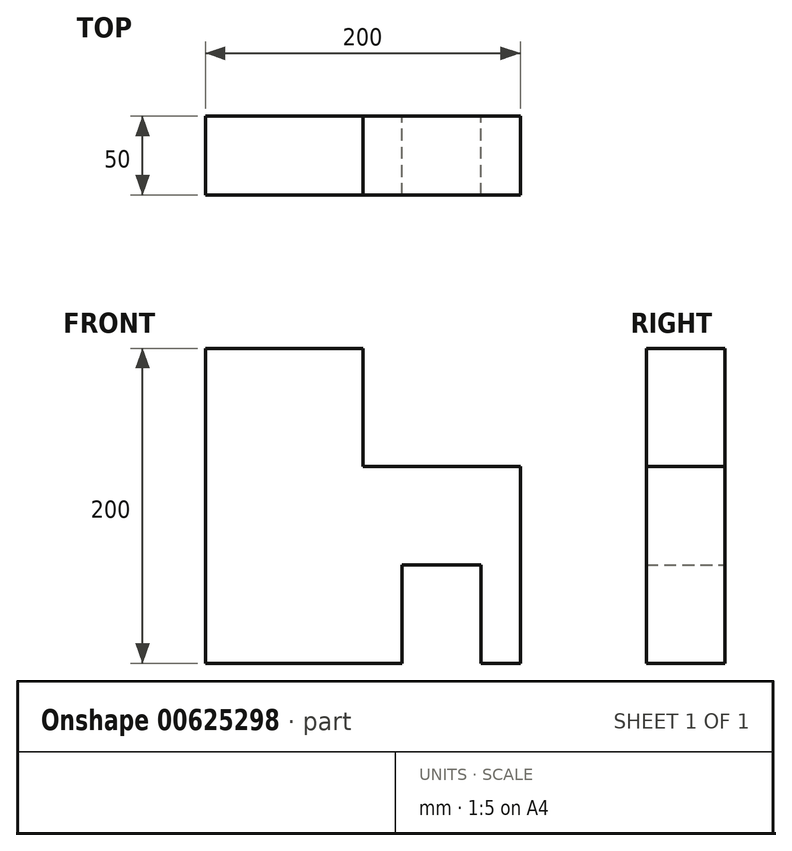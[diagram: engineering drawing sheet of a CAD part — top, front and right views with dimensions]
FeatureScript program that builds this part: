
annotation { "Feature Type Name" : "Feature", "Feature Type Description" : "" }
export const myFeature = defineFeature(function(context is Context, id is Id, definition is map)
    precondition{}
    {
        {
            var Q0;
            Q0=qCreatedBy(makeId("Front.planeOp"),FACE);
            var sketch = newSketch(context, id + "F0", { "sketchPlane" : qUnion([Q0])});
            skLineSegment(sketch, "E0", {"start": v(0, 0) * mm, "end": v(-125, 0) * mm});
            skLineSegment(sketch, "E1", {"start": v(-125, 0) * mm, "end": v(-125, 200) * mm});
            skLineSegment(sketch, "E2", {"start": v(-125, 200) * mm, "end": v(-25, 200) * mm});
            skLineSegment(sketch, "E3", {"start": v(-25, 200) * mm, "end": v(-25, 125) * mm});
            skLineSegment(sketch, "E4", {"start": v(-25, 125) * mm, "end": v(75, 125) * mm});
            skLineSegment(sketch, "E5", {"start": v(75, 125) * mm, "end": v(75, 0) * mm});
            skLineSegment(sketch, "E6", {"start": v(75, 0) * mm, "end": v(50, 0) * mm});
            skLineSegment(sketch, "E7", {"start": v(50, 0) * mm, "end": v(50, 62.5) * mm});
            skPoint(sketch, "E7.endSnap0", {"position": v(75, 62.5) * mm});
            skLineSegment(sketch, "E8", {"start": v(50, 62.5) * mm, "end": v(0, 62.5) * mm});
            skLineSegment(sketch, "E9", {"start": v(0, 62.5) * mm, "end": v(0, 0) * mm});
            skSolve(sketch);
        }
        {
            var Q0;
            Q0 = qSketchRegion(id + "F0", true);
            extrude(context, id + "F1", {"entities" : qUnion([Q0]), "depth" : 50 * mm, "offsetDistance" : 25 * mm});
        }
    });
